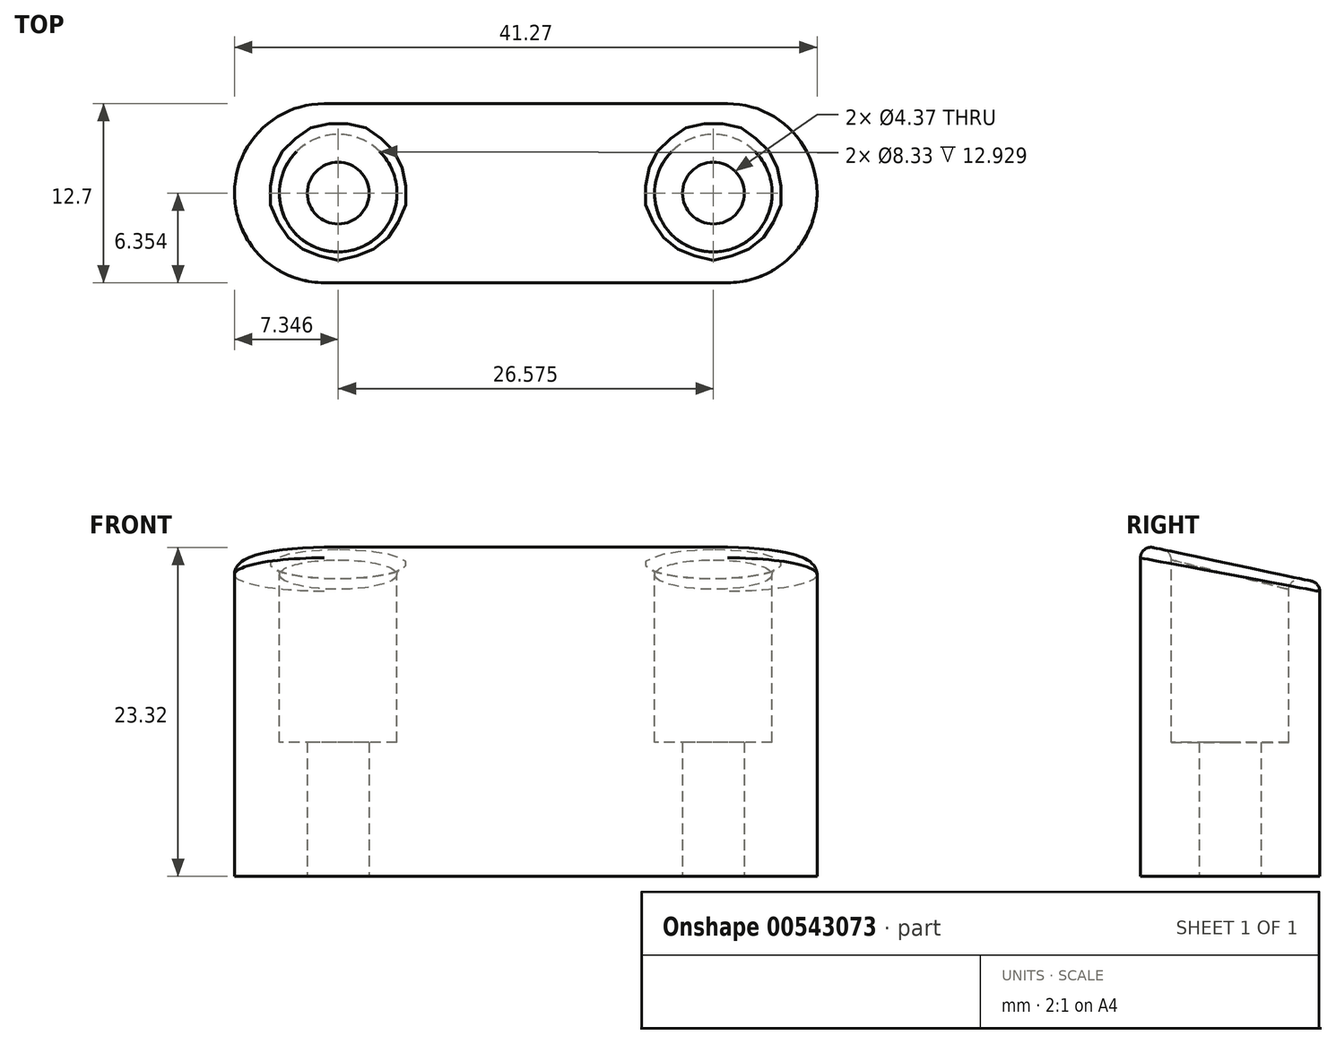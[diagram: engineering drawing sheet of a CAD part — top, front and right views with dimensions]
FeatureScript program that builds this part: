
annotation { "Feature Type Name" : "Feature", "Feature Type Description" : "" }
export const myFeature = defineFeature(function(context is Context, id is Id, definition is map)
    precondition{}
    {
        {
            var Q0;
            Q0=qCreatedBy(makeId("Top.planeOp"),FACE);
            var sketch = newSketch(context, id + "F0", { "sketchPlane" : qUnion([Q0])});
            skLineSegment(sketch, "E0.bottom", {"start": v(-19.9, 5.96) * mm, "end": v(21.38, 5.96) * mm});
            skLineSegment(sketch, "E0.top", {"start": v(-19.9, -6.74) * mm, "end": v(21.38, -6.74) * mm});
            skLineSegment(sketch, "E0.left", {"start": v(-19.9, 5.96) * mm, "end": v(-19.9, -6.74) * mm});
            skLineSegment(sketch, "E0.right", {"start": v(21.38, 5.96) * mm, "end": v(21.38, -6.74) * mm});
            skSolve(sketch);
        }
        {
            var Q0;
            Q0 = qSketchRegion(id + "F0", true);
            extrude(context, id + "F1", {"entities" : qUnion([Q0]), "depth" : 23.5 * mm, "offsetDistance" : 25 * mm});
        }
        {
            var Q0;
            Q0=makeQuery(id+"F1.opExtrude","CAP_FACE",FACE,{"disambiguationData":[OSD([sQuery(id+"F0.wireOp",EDGE,"E0.bottom"),sQuery(id+"F0.wireOp",EDGE,"E0.top"),sQuery(id+"F0.wireOp",EDGE,"E0.left"),sQuery(id+"F0.wireOp",EDGE,"E0.right")])],"isStart":true});
            var sketch = newSketch(context, id + "F2", { "sketchPlane" : qUnion([Q0])});
            skCircle(sketch, "E1", {"center": v(-12.54, 0.39) * mm, "radius": 2.18 * mm});
            skCircle(sketch, "E2", {"center": v(14.03, 0.39) * mm, "radius": 2.18 * mm});
            skSolve(sketch);
        }
        {
            var Q0;
            Q0 = qSketchRegion(id + "F2", true);
            extrude(context, id + "F3", {"entities" : qUnion([Q0]), "operationType" : NewBodyOperationType.REMOVE, "oppositeDirection" : true, "depth" : 25 * mm, "offsetDistance" : 25 * mm});
        }
        {
            var Q0;
            Q0=makeQuery(id+"F1.opExtrude","CAP_FACE",FACE,{"disambiguationData":[OSD([sQuery(id+"F0.wireOp",EDGE,"E0.bottom"),sQuery(id+"F0.wireOp",EDGE,"E0.top"),sQuery(id+"F0.wireOp",EDGE,"E0.left"),sQuery(id+"F0.wireOp",EDGE,"E0.right")])],"isStart":false});
            var sketch = newSketch(context, id + "F4", { "sketchPlane" : qUnion([Q0])});
            skCircle(sketch, "E3", {"center": v(-12.54, -0.39) * mm, "radius": 4.17 * mm});
            skCircle(sketch, "E4", {"center": v(14.03, -0.39) * mm, "radius": 4.17 * mm});
            skSolve(sketch);
        }
        {
            var Q0;
            Q0 = qSketchRegion(id + "F4", true);
            extrude(context, id + "F5", {"entities" : qUnion([Q0]), "operationType" : NewBodyOperationType.REMOVE, "oppositeDirection" : true, "depth" : 14 * mm, "offsetDistance" : 25 * mm});
        }
        {
            var Q0;
            Q0=makeQuery(id+"F1.opExtrude","CAP_EDGE",EDGE,{"disambiguationData":[OSD([sQuery(id+"F0.wireOp",EDGE,"E0.bottom")])],"isStart":false});
            chamfer(context, id + "F6", {"entities" : qUnion([Q0]), "chamferType" : ChamferType.OFFSET_ANGLE, "width" : 12.7 * mm, "oppositeDirection" : true, "angle" : 12 * degree, "tangentPropagation" : true});
        }
        {
            var Q0;
            Q0=makeQuery(id+"F1.opExtrude","SWEPT_EDGE",EDGE,{"disambiguationData":[OSD([sQuery(id+"F0.wireOp",EDGE,"E0.top"),sQuery(id+"F0.wireOp",EDGE,"E0.right")])]});
            var Q1;
            Q1=makeQuery(id+"F1.opExtrude","SWEPT_EDGE",EDGE,{"disambiguationData":[OSD([sQuery(id+"F0.wireOp",EDGE,"E0.bottom"),sQuery(id+"F0.wireOp",EDGE,"E0.right")])]});
            var Q2;
            Q2=makeQuery(id+"F1.opExtrude","SWEPT_EDGE",EDGE,{"disambiguationData":[OSD([sQuery(id+"F0.wireOp",EDGE,"E0.top"),sQuery(id+"F0.wireOp",EDGE,"E0.left")])]});
            var Q3;
            Q3=makeQuery(id+"F1.opExtrude","SWEPT_EDGE",EDGE,{"disambiguationData":[OSD([sQuery(id+"F0.wireOp",EDGE,"E0.bottom"),sQuery(id+"F0.wireOp",EDGE,"E0.left")])]});
            fillet(context, id + "F7", {"entities" : qUnion([Q0, Q1, Q2, Q3]), "radius" : 6.35 * mm, "tangentPropagation" : true, "allowEdgeOverflow" : false});
        }
        {
            var Q0;
            Q0=makeQuery(id+"F6.opChamfer","BLEND_FACE",FACE,{"disambiguationData":[OSD([sQuery(id+"F0.wireOp",EDGE,"E0.bottom")])]});
            fillet(context, id + "F8", {"entities" : qUnion([Q0]), "radius" : .75 * mm, "tangentPropagation" : true, "allowEdgeOverflow" : false});
        }
    });
